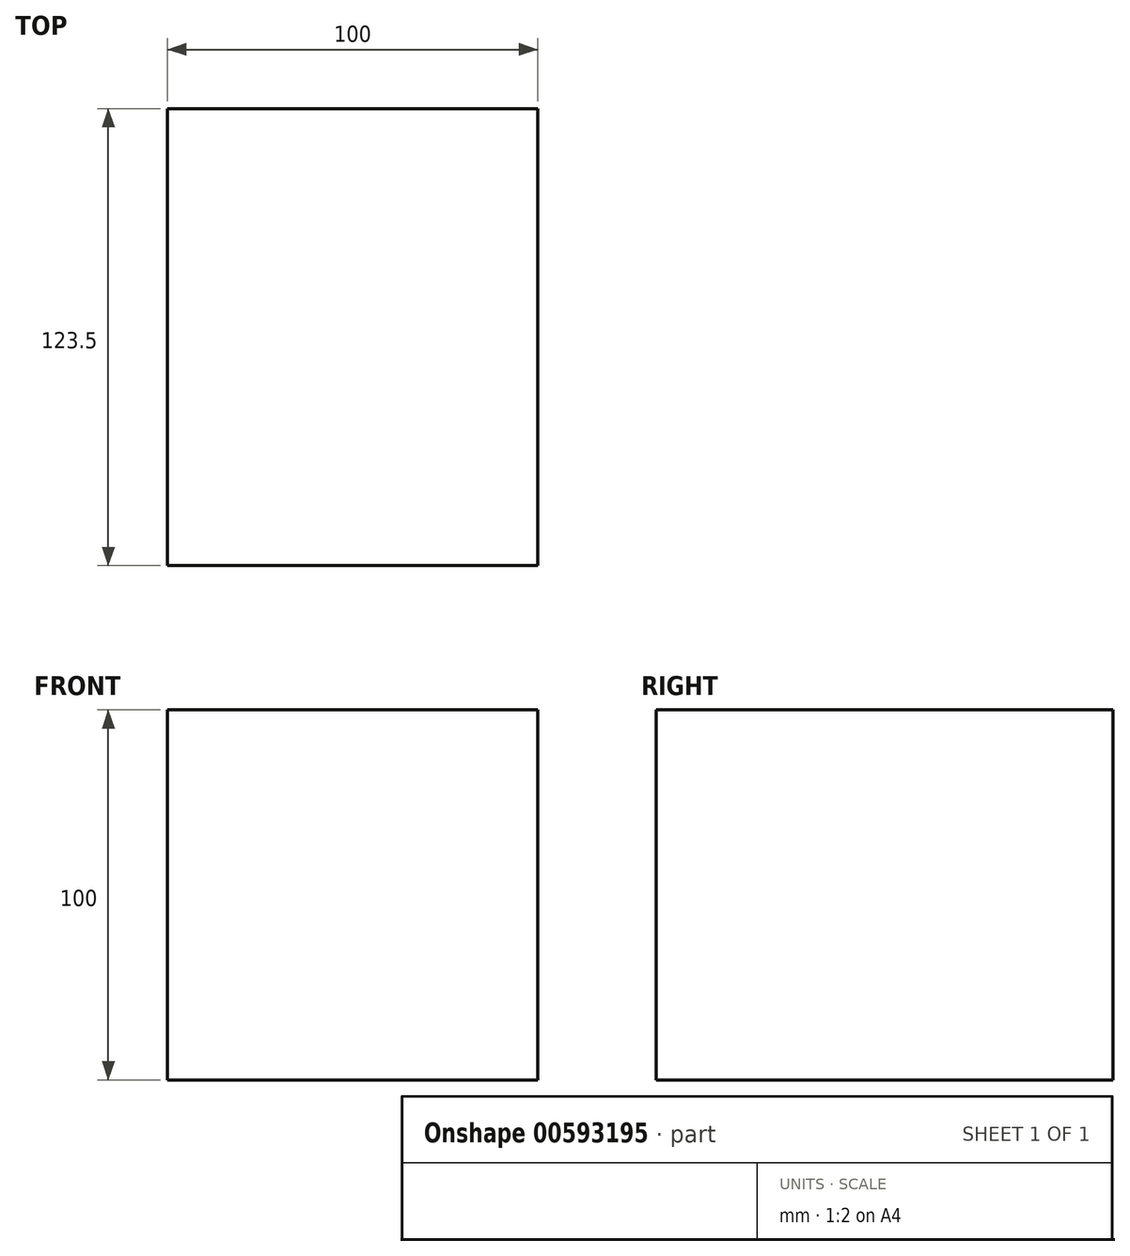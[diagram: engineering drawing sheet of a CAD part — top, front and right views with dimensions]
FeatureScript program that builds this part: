
annotation { "Feature Type Name" : "Feature", "Feature Type Description" : "" }
export const myFeature = defineFeature(function(context is Context, id is Id, definition is map)
    precondition{}
    {
        {
            var Q0;
            Q0=qCreatedBy(makeId("Front.planeOp"),FACE);
            var sketch = newSketch(context, id + "F0", { "sketchPlane" : qUnion([Q0])});
            skLineSegment(sketch, "E0.bottom", {"start": v(-50, -50) * mm, "end": v(50, -50) * mm});
            skLineSegment(sketch, "E0.top", {"start": v(-50, 50) * mm, "end": v(50, 50) * mm});
            skLineSegment(sketch, "E0.left", {"start": v(-50, -50) * mm, "end": v(-50, 50) * mm});
            skLineSegment(sketch, "E0.right", {"start": v(50, -50) * mm, "end": v(50, 50) * mm});
            skPoint(sketch, "E0.middle", {"position": v(0, 0) * mm});
            skSolve(sketch);
        }
        {
            var Q0;
            Q0=makeQuery(id+"F0.imprint","IMPRINT",FACE,{"disambiguationData":[TD([[makeQuery(id+"F0.imprint","IMPRINT",EDGE,{"derivedFrom":sQuery(id+"F0.wireOp",EDGE,"E0.bottom")}),1.0]])]});
            extrude(context, id + "F1", {"entities" : qUnion([Q0]), "depth" : 123.5 * mm, "offsetDistance" : 25 * mm});
        }
    });
